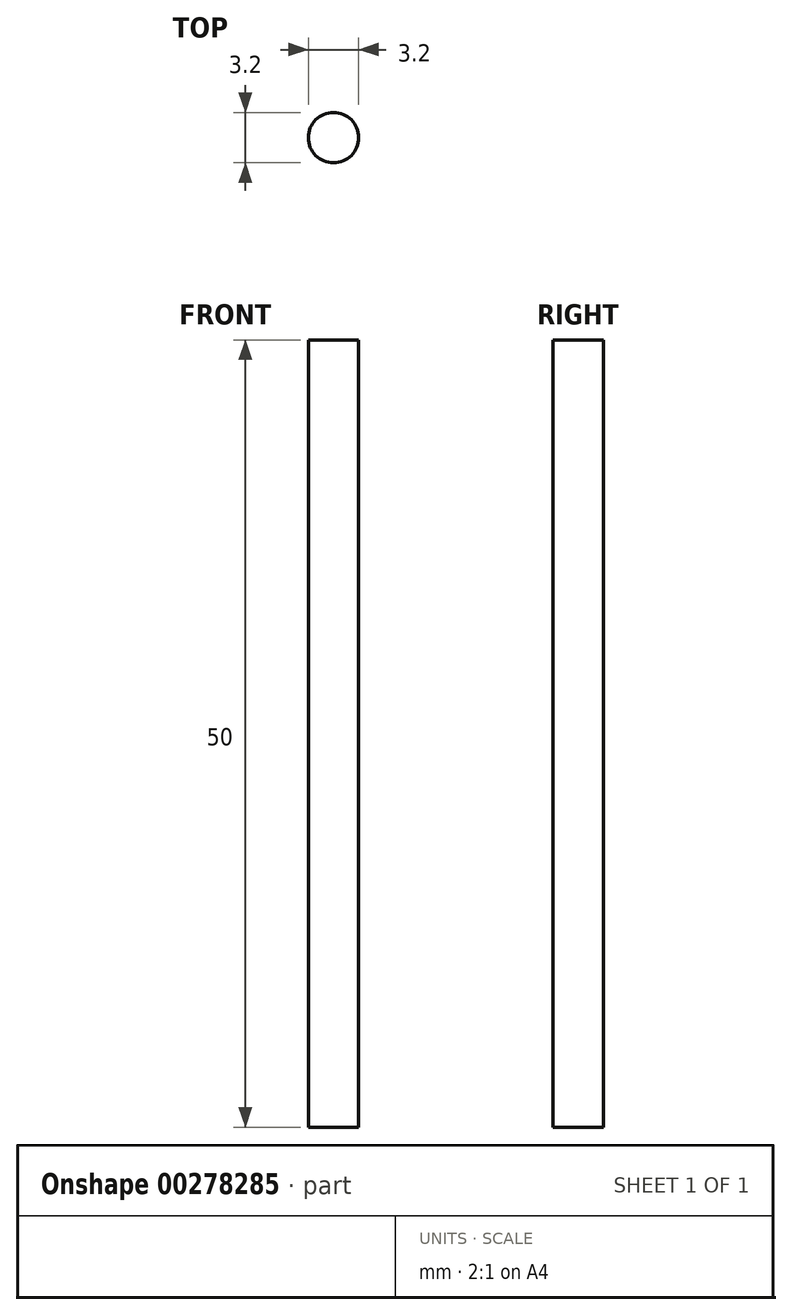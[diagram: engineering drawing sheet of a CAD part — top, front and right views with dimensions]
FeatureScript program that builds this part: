
annotation { "Feature Type Name" : "Feature", "Feature Type Description" : "" }
export const myFeature = defineFeature(function(context is Context, id is Id, definition is map)
    precondition{}
    {
        {
            var Q0;
            Q0=qCreatedBy(makeId("Top.planeOp"),FACE);
            var sketch = newSketch(context, id + "F0", { "sketchPlane" : qUnion([Q0])});
            skCircle(sketch, "E0", {"center": v(0, 0) * mm, "radius": 1.6 * mm});
            skSolve(sketch);
        }
        {
            var Q0;
            Q0 = qSketchRegion(id + "F0", true);
            extrude(context, id + "F1", {"entities" : qUnion([Q0]), "depth" : 50 * mm, "offsetDistance" : 25 * mm});
        }
    });
